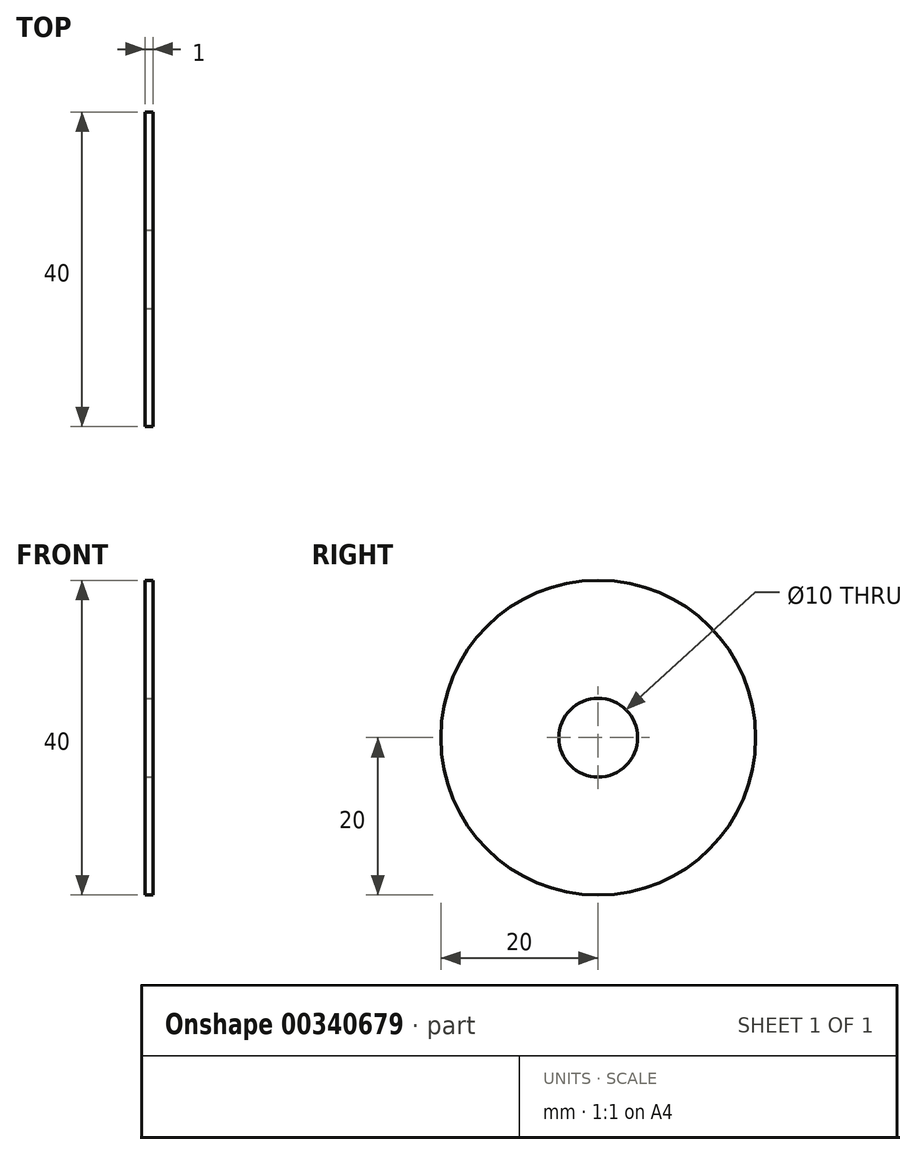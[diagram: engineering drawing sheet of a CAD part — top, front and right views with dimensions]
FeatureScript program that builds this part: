
annotation { "Feature Type Name" : "Feature", "Feature Type Description" : "" }
export const myFeature = defineFeature(function(context is Context, id is Id, definition is map)
    precondition{}
    {
        {
            var Q0;
            Q0=qCreatedBy(makeId("Right.planeOp"),FACE);
            var sketch = newSketch(context, id + "F0", { "sketchPlane" : qUnion([Q0])});
            skCircle(sketch, "E0", {"center": v(0, 0) * mm, "radius": 20 * mm});
            skSolve(sketch);
        }
        {
            var Q0;
            Q0 = qSketchRegion(id + "F0", true);
            extrude(context, id + "F1", {"entities" : qUnion([Q0]), "depth" : 1 * mm});
        }
        {
            var Q0;
            Q0=makeQuery(id+"F1.opExtrude","CAP_FACE",FACE,{"disambiguationData":[OSD([sQuery(id+"F0.wireOp",EDGE,"E0")])],"isStart":false});
            var sketch = newSketch(context, id + "F2", { "sketchPlane" : qUnion([Q0])});
            skCircle(sketch, "E1", {"center": v(0, 0) * mm, "radius": 2.47 * mm});
            skSolve(sketch);
        }
        {
            var Q0;
            Q0=sQuery(id+"F2.wireOp",VERTEX,"E1.center");
            var Q1;
            Q1=makeQuery(id+"F1.opExtrude","SWEPT_BODY",BODY,{"disambiguationData":[OSD([sQuery(id+"F0.wireOp",EDGE,"E0")])]});
            hole(context, id + "F3", {"style" : HoleStyle.SIMPLE, "endStyle" : HoleEndStyle.THROUGH, "holeDiameter" : 10 * mm, "isTappedThrough" : true, "tappedDepth" : 12 * mm, "tapClearance" : 3, "locations" : qUnion([Q0]), "scope" : qUnion([Q1])});
        }
    });
